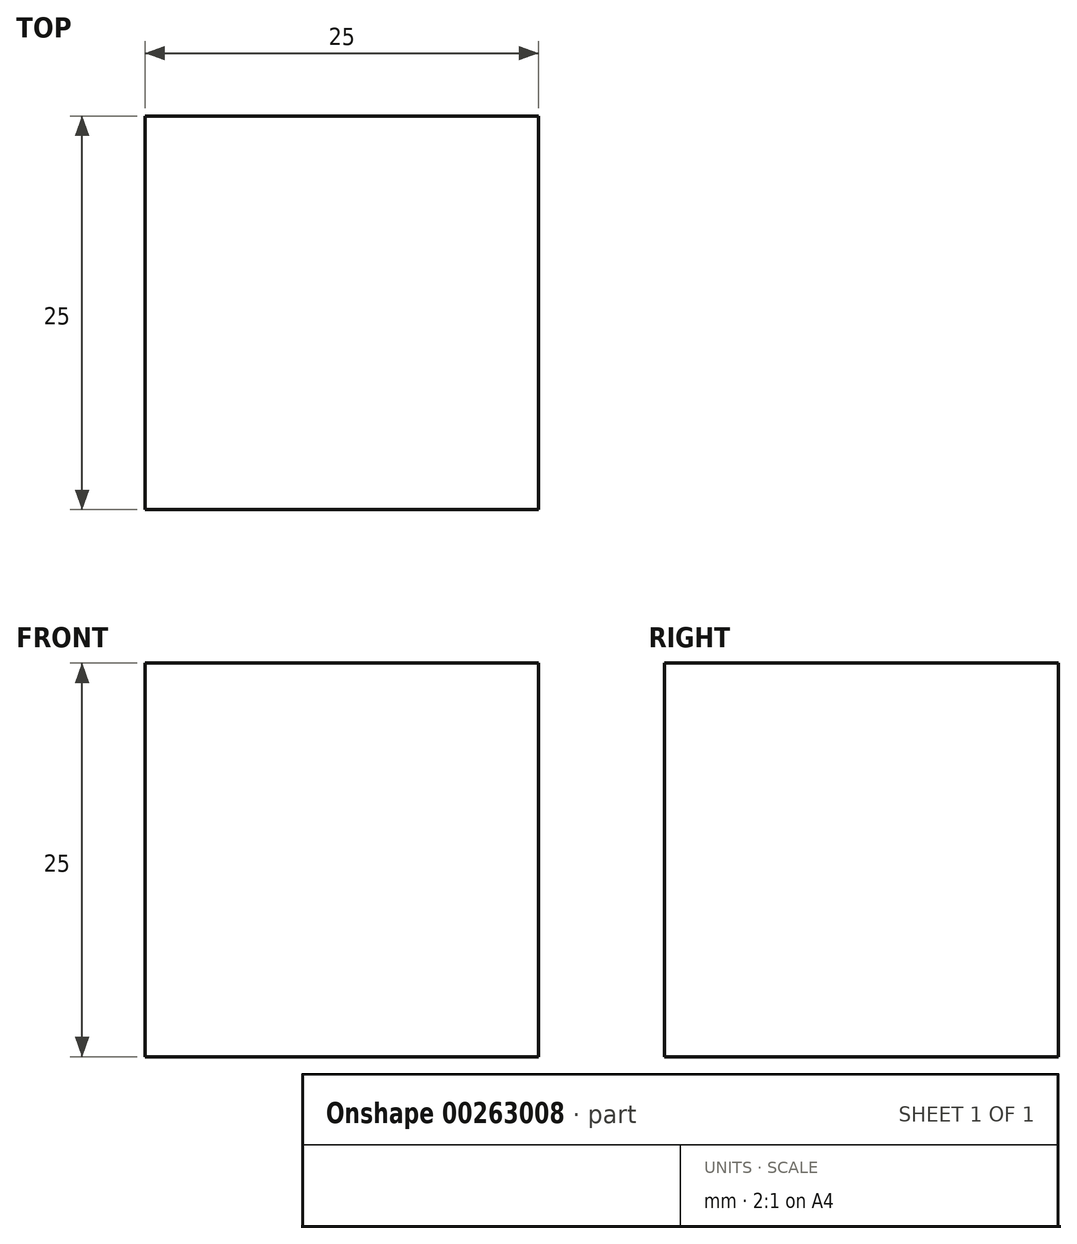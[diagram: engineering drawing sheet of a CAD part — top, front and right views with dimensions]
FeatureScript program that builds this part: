
annotation { "Feature Type Name" : "Feature", "Feature Type Description" : "" }
export const myFeature = defineFeature(function(context is Context, id is Id, definition is map)
    precondition{}
    {
        {
            var Q0;
            Q0=qCreatedBy(makeId("Top.planeOp"),FACE);
            var sketch = newSketch(context, id + "F0", { "sketchPlane" : qUnion([Q0])});
            skLineSegment(sketch, "E0.bottom", {"start": v(-12.5, -12.5) * mm, "end": v(12.5, -12.5) * mm});
            skLineSegment(sketch, "E0.top", {"start": v(-12.5, 12.5) * mm, "end": v(12.5, 12.5) * mm});
            skLineSegment(sketch, "E0.left", {"start": v(-12.5, -12.5) * mm, "end": v(-12.5, 12.5) * mm});
            skLineSegment(sketch, "E0.right", {"start": v(12.5, -12.5) * mm, "end": v(12.5, 12.5) * mm});
            skPoint(sketch, "E0.middle", {"position": v(0, 0) * mm});
            skSolve(sketch);
        }
        {
            var Q0;
            Q0=makeQuery(id+"F0.imprint","IMPRINT",FACE,{"disambiguationData":[TD([[makeQuery(id+"F0.imprint","IMPRINT",EDGE,{"derivedFrom":sQuery(id+"F0.wireOp",EDGE,"E0.bottom")}),1.0]])]});
            extrude(context, id + "F1", {"entities" : qUnion([Q0]), "depth" : 25 * mm});
        }
    });
